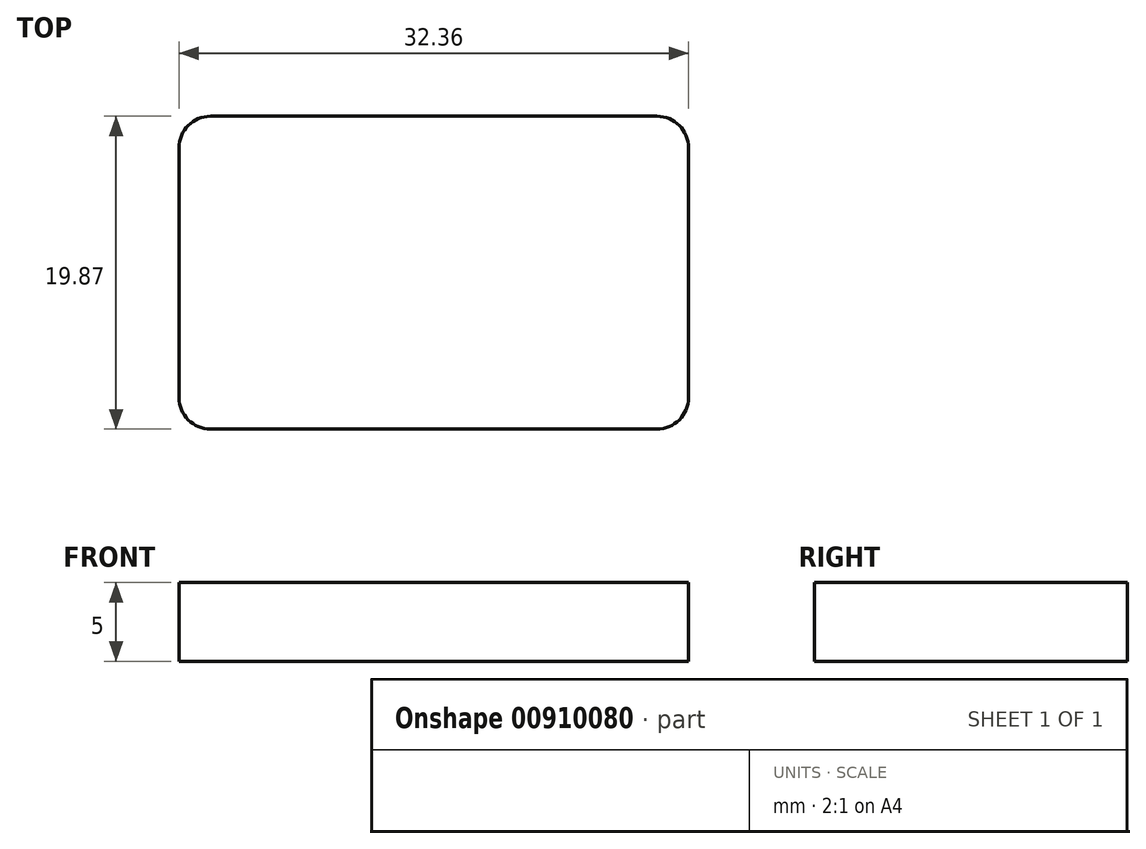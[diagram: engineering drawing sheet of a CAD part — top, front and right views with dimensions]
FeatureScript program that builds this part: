
annotation { "Feature Type Name" : "Feature", "Feature Type Description" : "" }
export const myFeature = defineFeature(function(context is Context, id is Id, definition is map)
    precondition{}
    {
        {
            var Q0;
            Q0=qCreatedBy(makeId("Top.planeOp"),FACE);
            var sketch = newSketch(context, id + "F0", { "sketchPlane" : qUnion([Q0])});
            skLineSegment(sketch, "E0.bottom", {"start": v(2.42, 9.62) * mm, "end": v(30.78, 9.62) * mm});
            skLineSegment(sketch, "E0.top", {"start": v(2.42, -10.25) * mm, "end": v(30.78, -10.25) * mm});
            skLineSegment(sketch, "E0.left", {"start": v(0.42, 7.62) * mm, "end": v(0.42, -8.25) * mm});
            skLineSegment(sketch, "E0.right", {"start": v(32.78, 7.62) * mm, "end": v(32.78, -8.25) * mm});
            skPoint(sketch, "E1.visualSharp", {"position": v(0.42, 9.62) * mm});
            skArc(sketch, "E1.filletArc", {"start": v(2.42, 9.62) * mm, "mid": v(1, 9.03) * mm, "end": v(0.42, 7.62) * mm});
            skPoint(sketch, "E2.visualSharp", {"position": v(32.78, 9.62) * mm});
            skArc(sketch, "E2.filletArc", {"start": v(32.78, 7.62) * mm, "mid": v(32.2, 9.03) * mm, "end": v(30.78, 9.62) * mm});
            skPoint(sketch, "E3.visualSharp", {"position": v(32.78, -10.25) * mm});
            skArc(sketch, "E3.filletArc", {"start": v(30.78, -10.25) * mm, "mid": v(32.2, -9.66) * mm, "end": v(32.78, -8.25) * mm});
            skPoint(sketch, "E4.visualSharp", {"position": v(0.42, -10.25) * mm});
            skArc(sketch, "E4.filletArc", {"start": v(0.42, -8.25) * mm, "mid": v(1, -9.66) * mm, "end": v(2.42, -10.25) * mm});
            skSolve(sketch);
        }
        {
            var Q0;
            Q0=makeQuery(id+"F0.imprint","IMPRINT",FACE,{"disambiguationData":[TD([[makeQuery(id+"F0.imprint","IMPRINT",EDGE,{"derivedFrom":sQuery(id+"F0.wireOp",EDGE,"E0.bottom")}),-1.0]])]});
            extrude(context, id + "F1", {"entities" : qUnion([Q0]), "depth" : 5 * mm, "offsetDistance" : 25 * mm});
        }
    });
